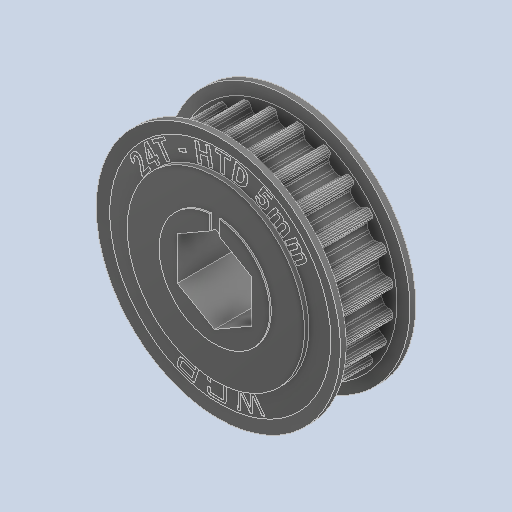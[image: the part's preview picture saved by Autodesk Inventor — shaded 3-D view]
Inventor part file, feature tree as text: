
AUTODESK INVENTOR PART (.ipt)
format: ipt  version: 2024 (Build 280153000, 153)  size: 869,888 bytes
history: native  units: in
note: dims shown in document units (in); Inventor stores cm internally (conversion verified against a paired STEP export)
features: mirror x2, other x1
ambient origin geometry x8: Origin, YZ Plane, XZ Plane, XY Plane, X Axis, Y Axis, Z Axis, Center Point
bodies: Solid1 (feature_tree), Solid2 (feature_tree), Solid3 (feature_tree)
feature tree (3):
  mirror  "Mirror2"
  mirror  "Mirror1"
  other  "Cut-Extrude5"
